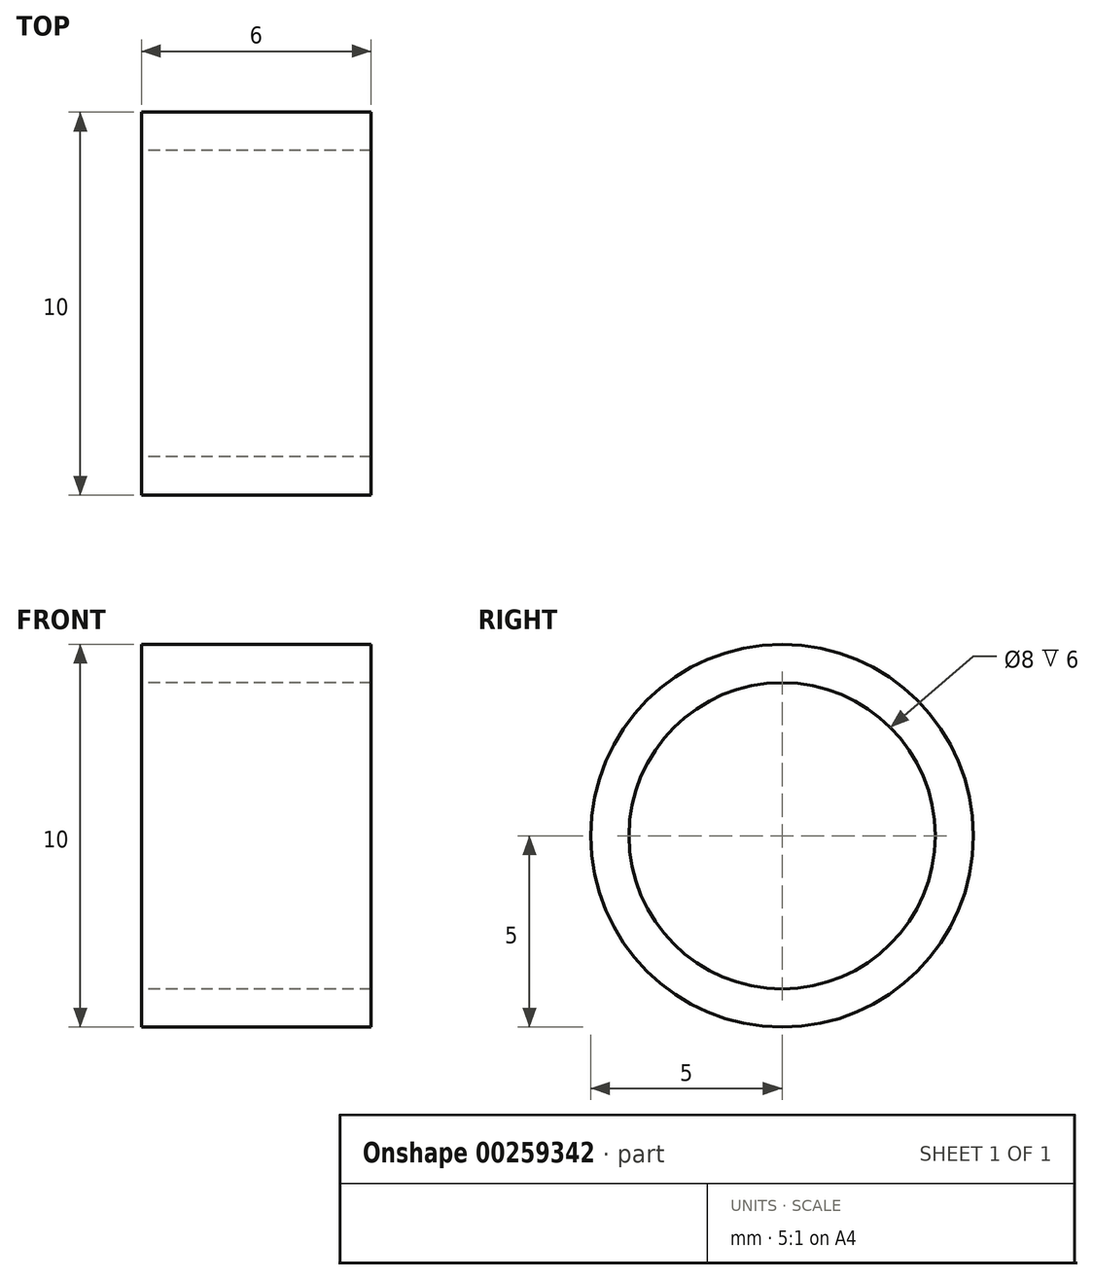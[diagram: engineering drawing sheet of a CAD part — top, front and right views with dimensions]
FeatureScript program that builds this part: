
annotation { "Feature Type Name" : "Feature", "Feature Type Description" : "" }
export const myFeature = defineFeature(function(context is Context, id is Id, definition is map)
    precondition{}
    {
        {
            var Q0;
            Q0=qCreatedBy(makeId("Front.planeOp"),FACE);
            var sketch = newSketch(context, id + "F0", { "sketchPlane" : qUnion([Q0])});
            skLineSegment(sketch, "E0", {"start": v(0, 4) * mm, "end": v(3, 4) * mm});
            skLineSegment(sketch, "E1", {"start": v(3, 4) * mm, "end": v(3, 5) * mm});
            skLineSegment(sketch, "E2", {"start": v(3, 5) * mm, "end": v(0, 5) * mm});
            skLineSegment(sketch, "E3", {"start": v(0, 5) * mm, "end": v(0, 4) * mm});
            skLineSegment(sketch, "E4", {"start": v(0, 0) * mm, "end": v(7.85, 0) * mm, "construction": true});
            skLineSegment(sketch, "E5.MirrorCS", {"start": v(-3, 5) * mm, "end": v(0, 5) * mm});
            skLineSegment(sketch, "E6.MirrorCS", {"start": v(-3, 4) * mm, "end": v(-3, 5) * mm});
            skLineSegment(sketch, "E7.MirrorCS", {"start": v(0, 4) * mm, "end": v(-3, 4) * mm});
            skSolve(sketch);
        }
        {
            var Q0;
            Q0=makeQuery(id+"F0.imprint","IMPRINT",FACE,{"disambiguationData":[TD([[makeQuery(id+"F0.imprint","IMPRINT",EDGE,{"derivedFrom":sQuery(id+"F0.wireOp",EDGE,"E5.MirrorCS")}),-1.0]])]});
            var Q1;
            Q1=makeQuery(id+"F0.imprint","IMPRINT",FACE,{"disambiguationData":[TD([[makeQuery(id+"F0.imprint","IMPRINT",EDGE,{"derivedFrom":sQuery(id+"F0.wireOp",EDGE,"E0")}),1.0]])]});
            var Q2;
            Q2=sQuery(id+"F0.wireOp",EDGE,"E4");
            revolve(context, id + "F1", {"entities" : qUnion([Q0, Q1]), "axis" : qUnion([Q2]), "revolveType" : RevolveType.FULL});
        }
    });
